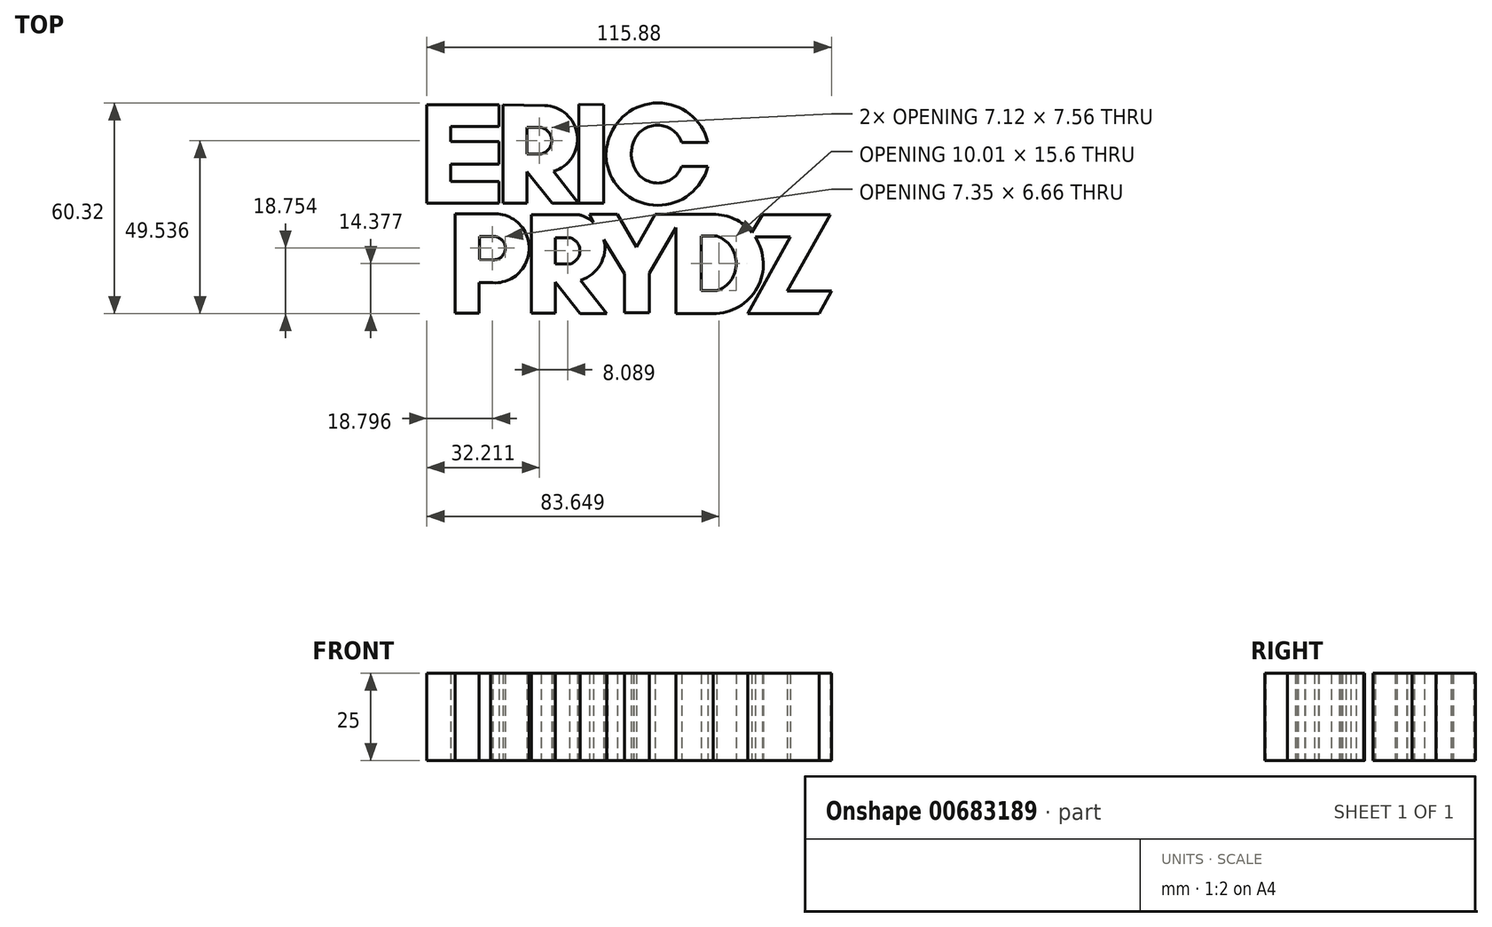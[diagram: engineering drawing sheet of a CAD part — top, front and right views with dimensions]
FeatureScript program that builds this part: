
annotation { "Feature Type Name" : "Feature", "Feature Type Description" : "" }
export const myFeature = defineFeature(function(context is Context, id is Id, definition is map)
    precondition{}
    {
        {
            var Q0;
            Q0=qCreatedBy(makeId("Top.planeOp"),FACE);
            var sketch = newSketch(context, id + "F0", { "sketchPlane" : qUnion([Q0])});
            skLineSegment(sketch, "E0", {"start": v(-80, 10.57) * mm, "end": v(-80, -17.58) * mm});
            skLineSegment(sketch, "E1", {"start": v(-80, -17.58) * mm, "end": v(-73.08, -17.58) * mm});
            skLineSegment(sketch, "E2", {"start": v(-73.08, -17.58) * mm, "end": v(-73.08, -8.63) * mm});
            skLineSegment(sketch, "E3", {"start": v(-73.08, -8.63) * mm, "end": v(-65.96, -17.66) * mm});
            skLineSegment(sketch, "E4", {"start": v(-65.96, -17.66) * mm, "end": v(-58.4, -17.66) * mm});
            skLineSegment(sketch, "E5", {"start": v(-58.4, -17.66) * mm, "end": v(-65.56, -8.55) * mm});
            skLineSegment(sketch, "E6", {"start": v(-73.17, 4.05) * mm, "end": v(-73.17, -3.5) * mm});
            skLineSegment(sketch, "E7", {"start": v(-73.17, -3.5) * mm, "end": v(-69.09, -3.5) * mm});
            skLineSegment(sketch, "E8", {"start": v(-73.17, 4.05) * mm, "end": v(-69.09, 4.05) * mm});
            skArc(sketch, "E9", {"start": v(-69.09, -3.5) * mm, "mid": v(-66.05, 0.28) * mm, "end": v(-69.09, 4.05) * mm});
            skArc(sketch, "E10", {"start": v(-65.56, -8.55) * mm, "mid": v(-58.74, 1.99) * mm, "end": v(-68.11, 10.33) * mm});
            skLineSegment(sketch, "E11", {"start": v(-80, 10.57) * mm, "end": v(-68.11, 10.33) * mm});
            skLineSegment(sketch, "E12", {"start": v(-58.34, 10.68) * mm, "end": v(-58.28, -17.66) * mm});
            skLineSegment(sketch, "E13", {"start": v(-58.28, -17.66) * mm, "end": v(-51.13, -17.65) * mm});
            skLineSegment(sketch, "E14", {"start": v(-51.13, -17.65) * mm, "end": v(-51.18, 10.58) * mm});
            skLineSegment(sketch, "E15", {"start": v(-51.18, 10.58) * mm, "end": v(-58.34, 10.68) * mm});
            skLineSegment(sketch, "E16", {"start": v(-28.87, -0.19) * mm, "end": v(-21.31, -0.19) * mm});
            skLineSegment(sketch, "E17", {"start": v(-21.32, -7.1) * mm, "end": v(-28.82, -7.1) * mm});
            skArc(sketch, "E18", {"start": v(-42.53, -7.1) * mm, "mid": v(-35.67, -11.87) * mm, "end": v(-28.82, -7.1) * mm});
            skArc(sketch, "E19", {"start": v(-28.87, -0.19) * mm, "mid": v(-35.75, 4.73) * mm, "end": v(-42.63, -0.19) * mm});
            skArc(sketch, "E20", {"start": v(-50.08, -7.1) * mm, "mid": v(-35.7, -18.22) * mm, "end": v(-21.32, -7.1) * mm});
            skArc(sketch, "E21", {"start": v(-21.31, -0.19) * mm, "mid": v(-35.64, 11.06) * mm, "end": v(-49.97, -0.19) * mm});
            skArc(sketch, "E22", {"start": v(-49.97, -0.19) * mm, "mid": v(-50.51, -3.63) * mm, "end": v(-50.08, -7.1) * mm});
            skArc(sketch, "E23", {"start": v(-42.63, -0.19) * mm, "mid": v(-43.26, -3.65) * mm, "end": v(-42.53, -7.1) * mm});
            skLineSegment(sketch, "E24", {"start": v(-101.82, -17.59) * mm, "end": v(-81.21, -17.59) * mm});
            skLineSegment(sketch, "E25", {"start": v(-81.21, -17.59) * mm, "end": v(-81.21, -11.45) * mm});
            skLineSegment(sketch, "E26", {"start": v(-81.21, -11.45) * mm, "end": v(-94.94, -11.45) * mm});
            skLineSegment(sketch, "E27", {"start": v(-94.94, -11.45) * mm, "end": v(-94.94, -6.42) * mm});
            skLineSegment(sketch, "E28", {"start": v(-94.94, -6.42) * mm, "end": v(-81.21, -6.42) * mm});
            skLineSegment(sketch, "E29", {"start": v(-81.21, -6.42) * mm, "end": v(-81.21, 0) * mm});
            skLineSegment(sketch, "E30", {"start": v(-81.21, 0) * mm, "end": v(-94.94, 0) * mm});
            skLineSegment(sketch, "E31", {"start": v(-81.21, 4.32) * mm, "end": v(-94.94, 4.32) * mm});
            skLineSegment(sketch, "E32", {"start": v(-94.94, 4.32) * mm, "end": v(-94.94, 0) * mm});
            skLineSegment(sketch, "E33", {"start": v(-81.21, 4.32) * mm, "end": v(-81.21, 10.5) * mm});
            skLineSegment(sketch, "E34", {"start": v(-81.21, 10.5) * mm, "end": v(-101.82, 10.5) * mm});
            skLineSegment(sketch, "E35", {"start": v(-101.82, 10.5) * mm, "end": v(-101.82, -17.59) * mm});
            skLineSegment(sketch, "E36", {"start": v(-93.72, -20.7) * mm, "end": v(-93.72, -49.13) * mm});
            skLineSegment(sketch, "E37", {"start": v(-93.72, -49.13) * mm, "end": v(-86.86, -49.13) * mm});
            skLineSegment(sketch, "E38", {"start": v(-86.86, -49.13) * mm, "end": v(-86.86, -40.36) * mm});
            skLineSegment(sketch, "E39", {"start": v(-86.86, -40.36) * mm, "end": v(-83.58, -40.36) * mm});
            skLineSegment(sketch, "E40", {"start": v(-93.72, -20.7) * mm, "end": v(-83.58, -20.7) * mm});
            skArc(sketch, "E41", {"start": v(-83.58, -40.36) * mm, "mid": v(-72.49, -30.53) * mm, "end": v(-83.58, -20.7) * mm});
            skArc(sketch, "E42", {"start": v(-82.93, -33.84) * mm, "mid": v(-79.35, -30.46) * mm, "end": v(-83.02, -27.18) * mm});
            skLineSegment(sketch, "E43", {"start": v(-83.02, -27.18) * mm, "end": v(-86.7, -27.18) * mm});
            skLineSegment(sketch, "E44", {"start": v(-86.7, -27.18) * mm, "end": v(-86.7, -33.8) * mm});
            skLineSegment(sketch, "E45", {"start": v(-86.7, -33.8) * mm, "end": v(-82.93, -33.84) * mm});
            skLineSegment(sketch, "E46", {"start": v(-71.92, -20.98) * mm, "end": v(-71.92, -49.13) * mm});
            skLineSegment(sketch, "E47", {"start": v(-71.92, -49.13) * mm, "end": v(-65, -49.13) * mm});
            skLineSegment(sketch, "E48", {"start": v(-65, -49.13) * mm, "end": v(-65, -40.18) * mm});
            skLineSegment(sketch, "E49", {"start": v(-65, -40.18) * mm, "end": v(-57.87, -49.22) * mm});
            skLineSegment(sketch, "E50", {"start": v(-57.87, -49.22) * mm, "end": v(-50.31, -49.22) * mm});
            skLineSegment(sketch, "E51", {"start": v(-50.31, -49.22) * mm, "end": v(-57.8, -39.69) * mm});
            skLineSegment(sketch, "E52", {"start": v(-65.08, -27.5) * mm, "end": v(-65.08, -35.06) * mm});
            skLineSegment(sketch, "E53", {"start": v(-65.08, -35.06) * mm, "end": v(-61, -35.06) * mm});
            skLineSegment(sketch, "E54", {"start": v(-65.08, -27.5) * mm, "end": v(-61, -27.5) * mm});
            skArc(sketch, "E55", {"start": v(-61, -35.06) * mm, "mid": v(-57.96, -31.28) * mm, "end": v(-61, -27.5) * mm});
            skArc(sketch, "E56", {"start": v(-57.8, -39.69) * mm, "mid": v(-50.85, -30.17) * mm, "end": v(-58.17, -20.94) * mm});
            skLineSegment(sketch, "E57", {"start": v(-71.92, -20.98) * mm, "end": v(-58.17, -20.94) * mm});
            skLineSegment(sketch, "E58", {"start": v(-30.53, -24.64) * mm, "end": v(-38.1, -37.7) * mm});
            skLineSegment(sketch, "E59", {"start": v(-38.1, -37.7) * mm, "end": v(-38.1, -48.96) * mm});
            skLineSegment(sketch, "E60", {"start": v(-38.1, -48.96) * mm, "end": v(-45.27, -48.96) * mm});
            skLineSegment(sketch, "E61", {"start": v(-45.27, -48.96) * mm, "end": v(-45.27, -37.86) * mm});
            skLineSegment(sketch, "E62", {"start": v(-45.27, -37.86) * mm, "end": v(-51.14, -27.98) * mm});
            skLineSegment(sketch, "E63", {"start": v(-54.1, -23.1) * mm, "end": v(-55.23, -20.85) * mm});
            skLineSegment(sketch, "E64", {"start": v(-55.23, -20.85) * mm, "end": v(-47.25, -20.85) * mm});
            skLineSegment(sketch, "E65", {"start": v(-47.25, -20.85) * mm, "end": v(-41.78, -30.18) * mm});
            skLineSegment(sketch, "E66", {"start": v(-41.78, -30.18) * mm, "end": v(-36.47, -20.85) * mm});
            skLineSegment(sketch, "E67", {"start": v(-36.47, -20.85) * mm, "end": v(-19.84, -20.85) * mm});
            skLineSegment(sketch, "E68", {"start": v(-30.53, -24.64) * mm, "end": v(-30.53, -49.2) * mm});
            skLineSegment(sketch, "E69", {"start": v(-30.53, -49.2) * mm, "end": v(-19.84, -49.2) * mm});
            skArc(sketch, "E70", {"start": v(-19.84, -20.85) * mm, "mid": v(-5.44, -35.03) * mm, "end": v(-19.84, -49.2) * mm});
            skLineSegment(sketch, "E71", {"start": v(-8.71, -25.97) * mm, "end": v(-5.68, -20.9) * mm});
            skLineSegment(sketch, "E72", {"start": v(-5.68, -20.9) * mm, "end": v(13.76, -20.97) * mm});
            skLineSegment(sketch, "E73", {"start": v(13.76, -20.97) * mm, "end": v(1.37, -42.81) * mm});
            skLineSegment(sketch, "E74", {"start": v(1.37, -42.81) * mm, "end": v(14.06, -42.81) * mm});
            skLineSegment(sketch, "E75", {"start": v(14.06, -42.81) * mm, "end": v(10.48, -49.26) * mm});
            skLineSegment(sketch, "E76", {"start": v(10.48, -49.26) * mm, "end": v(-9.88, -49.23) * mm});
            skLineSegment(sketch, "E77", {"start": v(-9.88, -49.23) * mm, "end": v(2.32, -27.3) * mm});
            skLineSegment(sketch, "E78", {"start": v(2.32, -27.3) * mm, "end": v(-7.74, -27.3) * mm});
            skLineSegment(sketch, "E79", {"start": v(-23.18, -27.08) * mm, "end": v(-23.18, -42.68) * mm});
            skLineSegment(sketch, "E80", {"start": v(-23.18, -42.68) * mm, "end": v(-18.78, -42.68) * mm});
            skLineSegment(sketch, "E81", {"start": v(-18.78, -27.08) * mm, "end": v(-23.18, -27.08) * mm});
            skArc(sketch, "E82", {"start": v(-18.78, -42.68) * mm, "mid": v(-13.16, -34.88) * mm, "end": v(-18.78, -27.08) * mm});
            skSolve(sketch);
        }
        {
            var Q0;
            Q0=makeQuery(id+"F0.imprint","IMPRINT",FACE,{"disambiguationData":[TD([[makeQuery(id+"F0.imprint","IMPRINT",EDGE,{"derivedFrom":sQuery(id+"F0.wireOp",EDGE,"E24")}),1.0]])]});
            var Q1;
            Q1=makeQuery(id+"F0.imprint","IMPRINT",FACE,{"disambiguationData":[TD([[makeQuery(id+"F0.imprint","IMPRINT",EDGE,{"derivedFrom":sQuery(id+"F0.wireOp",EDGE,"E0")}),1.0]])]});
            var Q2;
            Q2=makeQuery(id+"F0.imprint","IMPRINT",FACE,{"disambiguationData":[TD([[makeQuery(id+"F0.imprint","IMPRINT",EDGE,{"derivedFrom":sQuery(id+"F0.wireOp",EDGE,"E12")}),1.0]])]});
            var Q3;
            Q3=makeQuery(id+"F0.imprint","IMPRINT",FACE,{"disambiguationData":[TD([[makeQuery(id+"F0.imprint","IMPRINT",EDGE,{"derivedFrom":sQuery(id+"F0.wireOp",EDGE,"E16")}),1.0]])]});
            var Q4;
            Q4=makeQuery(id+"F0.imprint","IMPRINT",FACE,{"disambiguationData":[TD([[makeQuery(id+"F0.imprint","IMPRINT",EDGE,{"derivedFrom":sQuery(id+"F0.wireOp",EDGE,"E58")}),-1.0]])]});
            var Q5;
            Q5=makeQuery(id+"F0.imprint","IMPRINT",FACE,{"disambiguationData":[TD([[makeQuery(id+"F0.imprint","IMPRINT",EDGE,{"derivedFrom":sQuery(id+"F0.wireOp",EDGE,"E46")}),1.0]])]});
            var Q6;
            Q6=makeQuery(id+"F0.imprint","IMPRINT",FACE,{"disambiguationData":[TD([[makeQuery(id+"F0.imprint","IMPRINT",EDGE,{"derivedFrom":sQuery(id+"F0.wireOp",EDGE,"E36")}),1.0]])]});
            var Q7;
            {var subQ0=sQuery(id+"F0.wireOp",EDGE,"E71");Q7=makeQuery(id+"F0.imprint","IMPRINT",FACE,{"disambiguationData":[TD([[makeQuery(id+"F0.imprint","IMPRINT",EDGE,{"derivedFrom":subQ0}),-1.0]])]});}
            extrude(context, id + "F1", {"entities" : qUnion([Q0, Q1, Q2, Q3, Q4, Q5, Q6, Q7]), "depth" : 25 * mm, "offsetDistance" : 25 * mm});
        }
    });
